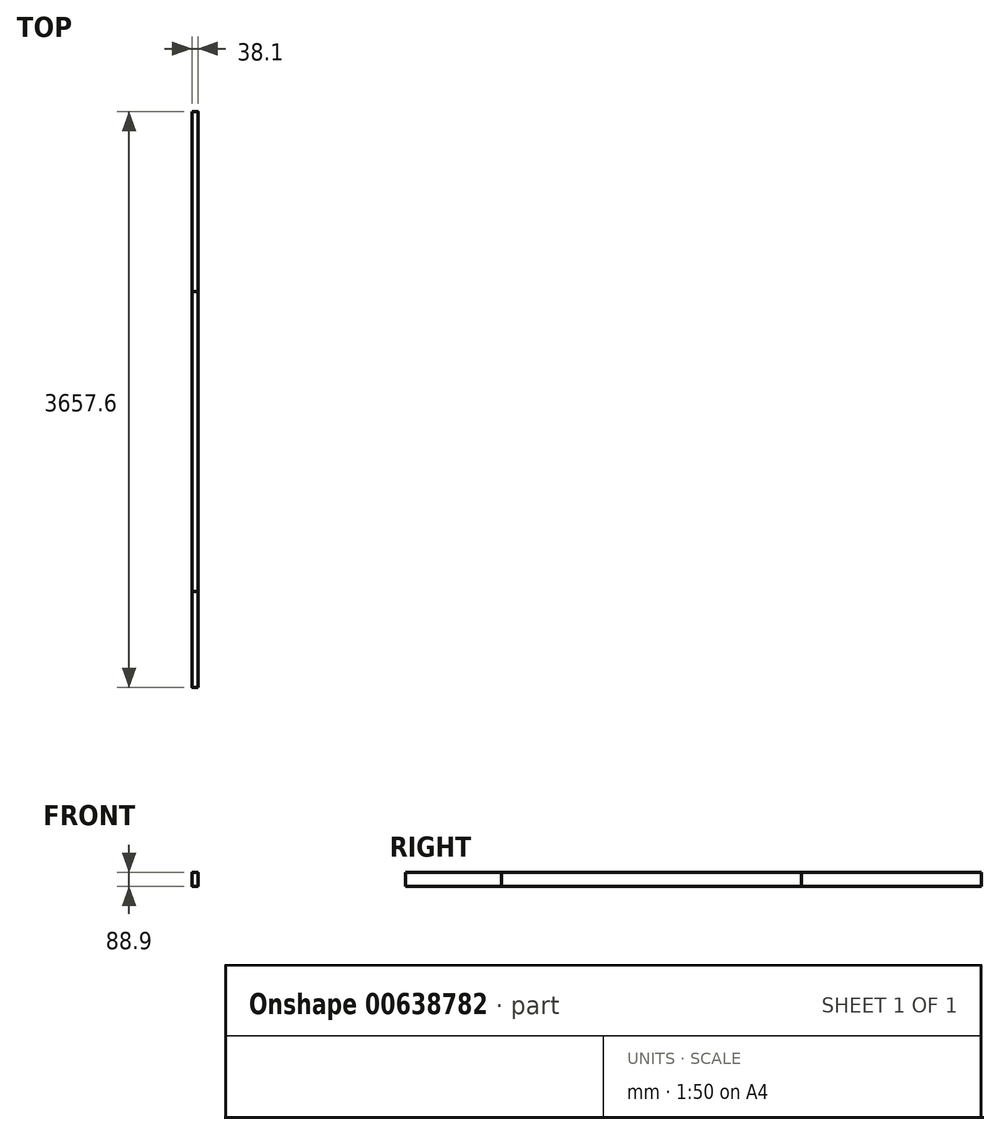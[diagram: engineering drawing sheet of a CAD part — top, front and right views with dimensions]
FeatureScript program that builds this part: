
annotation { "Feature Type Name" : "Feature", "Feature Type Description" : "" }
export const myFeature = defineFeature(function(context is Context, id is Id, definition is map)
    precondition{}
    {
        {
            var Q0;
            Q0=qCreatedBy(makeId("Front.planeOp"),FACE);
            var sketch = newSketch(context, id + "F0", { "sketchPlane" : qUnion([Q0])});
            skLineSegment(sketch, "E0.bottom", {"start": v(-15.87, 44.45) * mm, "end": v(15.88, 44.45) * mm});
            skLineSegment(sketch, "E0.top", {"start": v(-15.88, -44.45) * mm, "end": v(15.87, -44.45) * mm});
            skLineSegment(sketch, "E0.left", {"start": v(-19.05, 41.28) * mm, "end": v(-19.05, -41.27) * mm});
            skLineSegment(sketch, "E0.right", {"start": v(19.05, 41.28) * mm, "end": v(19.05, -41.27) * mm});
            skPoint(sketch, "E0.middle", {"position": v(0, 0) * mm});
            skPoint(sketch, "E1.visualSharp", {"position": v(-19.05, 44.45) * mm});
            skArc(sketch, "E1.filletArc", {"start": v(-15.87, 44.45) * mm, "mid": v(-18.12, 43.52) * mm, "end": v(-19.05, 41.28) * mm});
            skPoint(sketch, "E2.visualSharp", {"position": v(19.05, 44.45) * mm});
            skArc(sketch, "E2.filletArc", {"start": v(19.05, 41.28) * mm, "mid": v(18.12, 43.52) * mm, "end": v(15.88, 44.45) * mm});
            skPoint(sketch, "E3.visualSharp", {"position": v(19.05, -44.45) * mm});
            skArc(sketch, "E3.filletArc", {"start": v(15.87, -44.45) * mm, "mid": v(18.12, -43.52) * mm, "end": v(19.05, -41.27) * mm});
            skPoint(sketch, "E4.visualSharp", {"position": v(-19.05, -44.45) * mm});
            skArc(sketch, "E4.filletArc", {"start": v(-19.05, -41.27) * mm, "mid": v(-18.12, -43.52) * mm, "end": v(-15.88, -44.45) * mm});
            skLineSegment(sketch, "E5.left", {"start": v(-19.05, 41.27) * mm, "end": v(-19.05, -41.28) * mm});
            skLineSegment(sketch, "E5.right", {"start": v(19.05, 41.28) * mm, "end": v(19.05, -41.28) * mm});
            skArc(sketch, "E6.filletArc", {"start": v(15.87, -44.45) * mm, "mid": v(18.12, -43.52) * mm, "end": v(19.05, -41.28) * mm});
            skArc(sketch, "E7.filletArc", {"start": v(-19.05, -41.28) * mm, "mid": v(-18.12, -43.52) * mm, "end": v(-15.88, -44.45) * mm});
            skLineSegment(sketch, "E8.left", {"start": v(-19.05, 41.28) * mm, "end": v(-19.05, -41.28) * mm});
            skArc(sketch, "E9.filletArc", {"start": v(-15.87, 44.45) * mm, "mid": v(-18.12, 43.52) * mm, "end": v(-19.05, 41.27) * mm});
            skSolve(sketch);
        }
        {
            var Q0;
            Q0 = qSketchRegion(id + "F0", true);
            extrude(context, id + "F1", {"entities" : qUnion([Q0]), "depth" : 3657.6 * mm, "offsetDistance" : 25.4 * mm});
        }
        {
            var Q0;
            Q0 = qSketchRegion(id + "F0", true);
            extrude(context, id + "F2", {"entities" : qUnion([Q0]), "depth" : 1143 * mm, "offsetDistance" : 25.4 * mm});
        }
        {
            var Q0;
            Q0 = qSketchRegion(id + "F0", true);
            extrude(context, id + "F3", {"entities" : qUnion([Q0]), "depth" : 3048 * mm, "offsetDistance" : 25.4 * mm});
        }
    });
